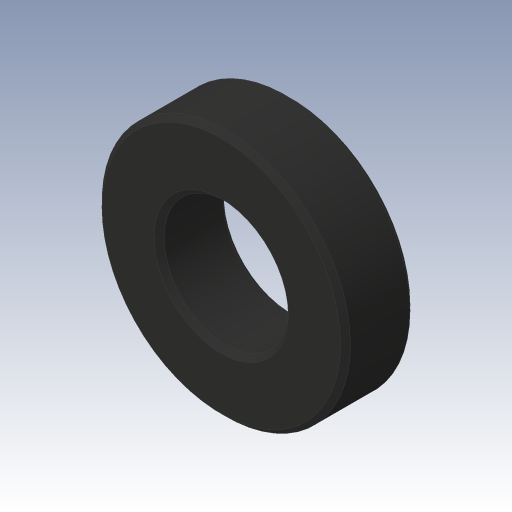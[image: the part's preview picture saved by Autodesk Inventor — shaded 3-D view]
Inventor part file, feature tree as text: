
AUTODESK INVENTOR PART (.ipt)
format: ipt  version: 2023.3 (Build 273359000, 359)  size: 144,384 bytes
history: native  units: in
note: dims shown in document units (in); Inventor stores cm internally (conversion verified against a paired STEP export)
features: extrude x1, chamfer x1, sketch x1
ambient origin geometry x8: Origin, YZ Plane, XZ Plane, XY Plane, X Axis, Y Axis, Z Axis, Center Point
bodies: Body1 (feature_tree)
feature tree (3):
  extrude  "Extrusion3"  Depth=0.3937in
  chamfer  "Fase1"  Distance=0.1102in
  sketch  "Skizze3"  dims[d4=0.1969in d5=0.3937in d6=0.1102in d7=0.0in d8=0.0079in d9=0.0787in d10=45.0deg]
